# Revit family: Countertop washbasin 1600x500x165 - Ilbagnoalessi one - Laufen - 814971
name_source: partatom
category: Plumbing Fixtures
revit_build: Autodesk Revit 2014 (Build: 20130308_1515(x64)
units: mm (PartAtom-declared; Revit-internal decimal feet)

## types (2) — shared parameters
BIMobject category = Basins
Date of publishing = 1/2/2012
Description = Countertop washbasin
Design country = Switzerland
Drain Diameter = 46 mm  [stored 0.150919 ft]
Edition number = 2
IFC Classification = Sanitary Terminal
Installation instructions = http://www.export.laufen.com
Manufacturer country = Austria
Manufacturer name = LAUFEN
Material main = Vitreous china
NBS Reference Code = 35-65-70-94
NBS Reference Description = Wash Basin Systems
Nominal height = 165
Nominal width = 1600
Option 01 = 104 : one tap hole, centre
Option 02 = 109 : without taphole
Options = 104 : one tap hole, centre
Product Guid = 235c3229-007f-4122-a3de-73db098ff738
Product certification = http://www.export.laufen.com
Product data url = http://bimobject.com
Product family = ILBAGNOALESSI ONE
Product group = Basins
QR code = http://bimobject.com
Secondary Material = Chrome - Ilbagnoalessi one - Laufen
Technical description = http://www.export.laufen.com
URL = http://www.export.laufen.com
Uniclass 1.4 Code = L7212
Uniclass 1.4 Description = Washbasins
Uniclass 2.0 Code = SS-35-65-70-94
Uniclass 2.0 Description = Wash Basin Systems
Weight Net (Kg) = 35.5

## per-type parameters (varying)
| type | Primary Material | Product SKU | Visibility Option 01 | Visibility Option 02 |
| 814971400 White with LCC | White with LCC - Ilbagnoalessi one - Laufen | 8149714001041 | No | Yes |
| 814971000 White | White - Ilbagnoalessi one - Laufen | 8149710001041 | Yes | No |

note: [stored X ft] marks values corroborated as IEEE doubles in the binary element streams (Revit-internal decimal feet)

## geometry (parser evidence)
native form markers: Sweep x6
no freeform markers — native parametric forms only
